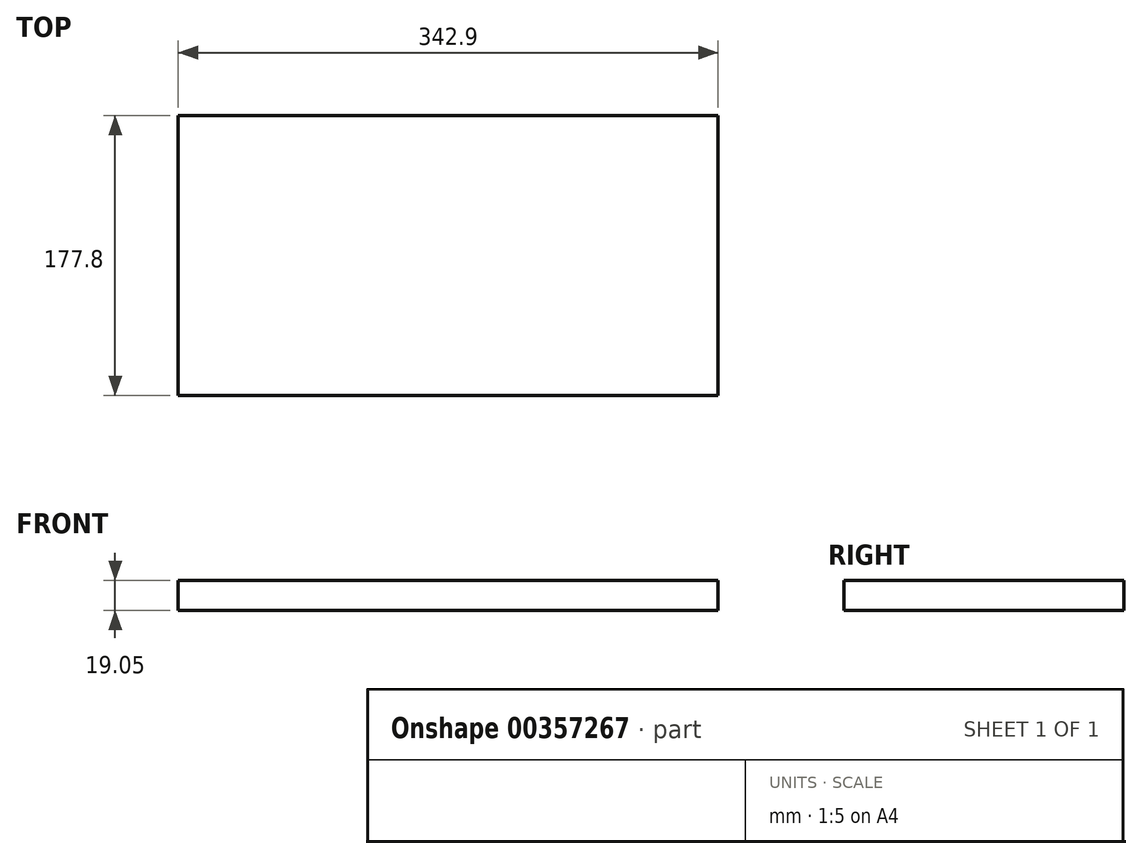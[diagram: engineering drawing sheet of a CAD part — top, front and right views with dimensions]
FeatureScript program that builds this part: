
annotation { "Feature Type Name" : "Feature", "Feature Type Description" : "" }
export const myFeature = defineFeature(function(context is Context, id is Id, definition is map)
    precondition{}
    {
        {
            var Q0;
            Q0=qCreatedBy(makeId("Top.planeOp"),FACE);
            var sketch = newSketch(context, id + "F0", { "sketchPlane" : qUnion([Q0])});
            skLineSegment(sketch, "E0.bottom", {"start": v(0, 0) * mm, "end": v(342.9, 0) * mm});
            skLineSegment(sketch, "E0.top", {"start": v(0, 177.8) * mm, "end": v(342.9, 177.8) * mm});
            skLineSegment(sketch, "E0.left", {"start": v(0, 0) * mm, "end": v(0, 177.8) * mm});
            skLineSegment(sketch, "E0.right", {"start": v(342.9, 0) * mm, "end": v(342.9, 177.8) * mm});
            skSolve(sketch);
        }
        {
            var Q0;
            Q0 = qSketchRegion(id + "F0", true);
            extrude(context, id + "F1", {"entities" : qUnion([Q0]), "depth" : 19.05 * mm});
        }
    });
